# Revit family: ITK_Патч-панель_Настенный монтаж_Неэкранированная
name_source: partatom
category: Обобщенные модели
units: mm (PartAtom-declared; Revit-internal decimal feet)

## family parameters
Всегда вертикально = Да
Может служить основой для арматурных стержней = Нет
На основе рабочей плоскости = Нет
Общий = Нет
При загрузке вырезать с полостями = Нет
Размер круглого соединителя = Использовать диаметр
Тип детали = Нормальный
Точка расчета площади = Нет

## types (2) — shared parameters
ADSK_URL страницы изделия = https://www.itk-group.ru
ADSK_Версия Revit = 2019
ADSK_Версия семейства = 1.0
ADSK_Группирование = I. ЩИТЫ И ПУЛЬТЫ
ADSK_Единица измерения = шт
ADSK_Завод-изготовитель = IEK
ADSK_Масса = 0.4
ADSK_Материал наименование = АБС-пластик
IEK_URL = https://www.itk-group.ru
IEK_Описание = Соответствие международным стандартам и ГОСТ Р.
Монтаж как на стену.
Двойная понятная маркировка IDC-модулей и портов.
Расширенный частотный диапазон работы.
Увеличенное количество циклов включения-отключения.
Подходят для кабелей и патч-кордов диаметром 22-26 AWG всех производителей.
Применимы для сетей ISDN, 10baseT, 100baseT, 1000baseT, EIA RS 232/485, 155 Mbit ATM, Token Ring.
KSI_CPr_Строительные изделия = 27.12.31.61.1.04.09-1090
URL = https://www.iek.ru
Высота = 60 мм
Глубина = 48 мм
Изготовитель = ITK
Материал = Окраска - RAL 9005
Ширина = 253 мм

## per-type parameters (varying)
| type | ADSK_Код изделия | ADSK_Наименование | IEK_Цена за единицу |
| PP24-1UC5EU-D05 | PP12-C5EU-D05 | ITK Настенная патч-панель кат.5Е UTP, 12 портов (IDC Dual) | 1391.62 |
| PP12-C6U-D05 | PP12-C6U-D05 | ITK Настенная патч-панель кат.6 UTP, 12 портов (IDC Dual) | 1156.24 |
